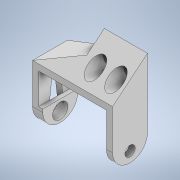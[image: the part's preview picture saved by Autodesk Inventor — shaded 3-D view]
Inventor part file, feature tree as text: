
AUTODESK INVENTOR PART (.ipt)
format: ipt  version: 2022.2 (Build 262287010, 287A)  size: 218,624 bytes
history: native  units: mm
features: extrude x10, sketch x10, fillet x1
ambient origin geometry x8: Origin, YZ Plane, XZ Plane, XY Plane, X Axis, Y Axis, Z Axis, Center Point
bodies: Solid1 (feature_tree)
feature tree (21):
  extrude  "Extrusion1"  Depth=5.0mm
  extrude  "Extrusion2"  Depth=3.0mm
  extrude  "Extrusion3"  Depth=17.0mm
  extrude  "Extrusion4"  Depth=14.0mm
  extrude  "Extrusion5"  Depth=15.0mm
  extrude  "Extrusion6"  Depth=10.0mm TaperAngle=0.0deg
  extrude  "Extrusion7"  Depth=17.0mm
  extrude  "Extrusion8"  Depth=7.0mm
  extrude  "Extrusion9"  Depth=5.0mm
  fillet  "Fillet1"  Radius=8.5mm
  extrude  "Extrusion10"  Depth=14.0mm TaperAngle=0.0deg
  sketch  "Sketch1"  dims[d0=5.0mm d1=25.0mm]
  sketch  "Sketch2"  dims[d2=3.0mm d3=25.0mm]
  sketch  "Sketch3"  dims[d4=31.0mm d6=17.0mm]
  sketch  "Sketch4"  dims[d7=17.0mm d8=0.0mm d9=14.0mm]
  sketch  "Sketch5"  dims[d10=17.0mm d11=0.0mm d12=15.0mm]
  sketch  "Sketch6"  dims[d13=13.0mm d14=10.0mm d15=0.0mm]
  sketch  "Sketch7"  dims[d16=20.0mm d17=17.0mm]
  sketch  "Sketch8"  dims[d18=7.0mm d19=7.0mm]
  sketch  "Sketch9"  dims[d20=8.5mm d21=5.0mm d22=8.5mm]
  sketch  "Sketch10"  dims[d23=5.0mm d24=14.0mm d25=0.0mm d26=3.0mm d27=3.0mm d28=14.0mm d29=0.0mm d30=10.0mm d31=0.0mm d32=18.0mm d33=7.0mm d34=7.0mm d35=10.0mm d36=0.0mm d37=7.5mm d38=5.0mm d39=8.5mm d40=10.0mm d41=0.0mm d42=5.0mm d43=5.0mm d44=8.5mm d45=10.0mm d46=0.0mm d47=8.5mm d48=0.0mm d49=4.0mm d50=15.0mm d51=0.0mm d52=3.0mm d53=0.0mm d54=2.0mm d55=15.0mm]
